# Revit family: Storage Tank Vert Round RGA257-940
name_source: partatom
category: Mechanical Equipment
revit_build: Autodesk Revit 2017 (Build: 20190507_1515(x64)
units: mm (PartAtom-declared; Revit-internal decimal feet)

## family parameters
Always vertical = Yes
Cut with Voids When Loaded = No
OmniClass Number = 23.65.35.11.17
OmniClass Title = Thermodynamic Water Heaters
Part Type = Normal
Room Calculation Point = No
Round Connector Dimension = Use Radius
Shared = No
Work Plane-Based = No

## types (7) — shared parameters
Description = Vertical Round Jacketed ASME Tanks
Drain Radius = 1/2"
Manufacturer = Lochinvar
NPT CONN SIZE = 3"
NPT Conn Radius = 1 1/2"
NPT OUTLET SIZE = 2"
NPT Outlet Conn Radius = 1"
SES BIM Studio # = 201264901-29
Top Clearance = 12"
URL = http://www.lochinvar.com

## per-type parameters (varying)
| type | A_TANK HEIGHT | B_TANK DIAMETER | D_NPT Height | E_NPT Height | GALLON CAPACITY | MODEL NO. | Manway | Manway Front Face from CL | Model | Pipe Extrusion Length | Tank Radius |
| RJA0257 | 91" | 34" | 18" | 26" | 257 | RJA257 | No | 19 1/2" | RJA257 | 19" | 17" |
| RJA0318 | 80" | 40" | 19 1/2" | 27 1/2" | 318 | RJA0318 | No | 22 1/2" | RJA0318 | 22" | 20" |
| RJA0432 | 80" | 46" | 21" | 29" | 432 | RJA0432 | Yes | 25 1/2" | RJA0432 | 25" | 23" |
| RJA0504 | 92" | 46" | 21" | 29" | 504 | RJA0504 | Yes | 25 1/2" | RJA0504 | 25" | 23" |
| RJA0650 | 92" | 52" | 23 1/2" | 31 1/2" | 650 | RJA0650 | Yes | 28 1/2" | RJA0650 | 28" | 26" |
| RJA0752 | 104" | 52" | 23 1/2" | 31 1/2" | 752 | RJA0752 | Yes | 28 1/2" | RJA0752 | 28" | 26" |
| RJA0940 | 128" | 52" | 23 1/2" | 31 1/2" | 940 | RJA0940 | Yes | 28 1/2" | RJA0940 | 28" | 26" |

## geometry (parser evidence)
native form markers: Extrusion x1, Sweep x2
no freeform markers — native parametric forms only
